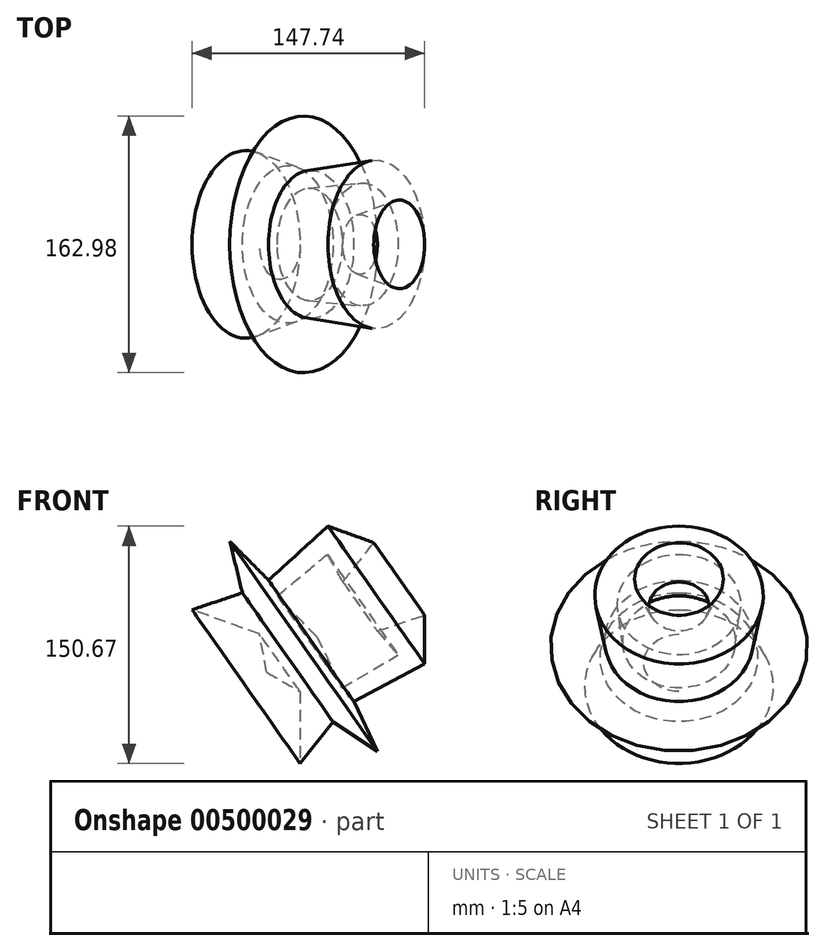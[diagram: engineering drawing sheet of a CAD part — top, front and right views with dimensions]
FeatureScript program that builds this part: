
annotation { "Feature Type Name" : "Feature", "Feature Type Description" : "" }
export const myFeature = defineFeature(function(context is Context, id is Id, definition is map)
    precondition{}
    {
        {
            var Q0;
            Q0=qCreatedBy(makeId("Front.planeOp"),FACE);
            var sketch = newSketch(context, id + "F0", { "sketchPlane" : qUnion([Q0])});
            skLineSegment(sketch, "E0", {"start": v(-55.37, 23.1) * mm, "end": v(-23.52, 45.47) * mm});
            skLineSegment(sketch, "E1", {"start": v(-23.52, 45.47) * mm, "end": v(-7.46, 13.05) * mm});
            skLineSegment(sketch, "E2", {"start": v(-7.46, 13.05) * mm, "end": v(28.11, 34) * mm});
            skLineSegment(sketch, "E3", {"start": v(28.11, 34) * mm, "end": v(14.92, 49.2) * mm});
            skLineSegment(sketch, "E4", {"start": v(14.92, 49.2) * mm, "end": v(45.04, 59.24) * mm});
            skLineSegment(sketch, "E5", {"start": v(45.04, 59.24) * mm, "end": v(45.04, 28.26) * mm});
            skLineSegment(sketch, "E6", {"start": v(45.04, 28.26) * mm, "end": v(0, 4.45) * mm});
            skLineSegment(sketch, "E7", {"start": v(0, 4.45) * mm, "end": v(14.92, -27.11) * mm});
            skLineSegment(sketch, "E8", {"start": v(14.92, -27.11) * mm, "end": v(-13.2, -8.46) * mm});
            skLineSegment(sketch, "E9", {"start": v(-13.2, -8.46) * mm, "end": v(-34.14, -34.86) * mm});
            skLineSegment(sketch, "E10", {"start": v(-34.14, -34.86) * mm, "end": v(-34.14, -5.02) * mm});
            skLineSegment(sketch, "E11", {"start": v(-34.14, -5.02) * mm, "end": v(-34.14, 10.76) * mm});
            skLineSegment(sketch, "E12", {"start": v(-34.14, 10.76) * mm, "end": v(-55.37, 23.1) * mm});
            skSolve(sketch);
        }
        {
            var Q0;
            Q0=makeQuery(id+"F0.imprint","IMPRINT",FACE,{"disambiguationData":[TD([[makeQuery(id+"F0.imprint","IMPRINT",EDGE,{"derivedFrom":sQuery(id+"F0.wireOp",EDGE,"E0")}),-1.0]])]});
            var Q1;
            Q1=sQuery(id+"F0.wireOp",EDGE,"E0");
            revolve(context, id + "F1", {"entities" : qUnion([Q0]), "axis" : qUnion([Q1]), "revolveType" : RevolveType.FULL});
        }
    });
